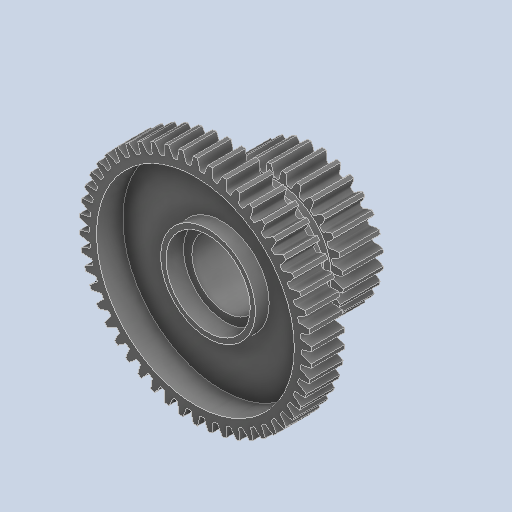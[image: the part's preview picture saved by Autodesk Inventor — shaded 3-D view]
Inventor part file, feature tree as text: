
AUTODESK INVENTOR PART (.ipt)
format: ipt  version: 2024.2 (Build 282272000, 272)  size: 733,696 bytes
history: native  units: in
note: dims shown in document units (in); Inventor stores cm internally (conversion verified against a paired STEP export)
features: chamfer x1
ambient origin geometry x8: Origin, YZ Plane, XZ Plane, XY Plane, X Axis, Y Axis, Z Axis, Center Point
bodies: Solid1 (feature_tree)
feature tree (1):
  chamfer  "Chamfer1"  [1 undecoded]
note: 1 required parameter value undecoded (feature->parameter linkage not recoverable at this tier; creation-order binding heuristic only, values carry confidence <= 0.55)
